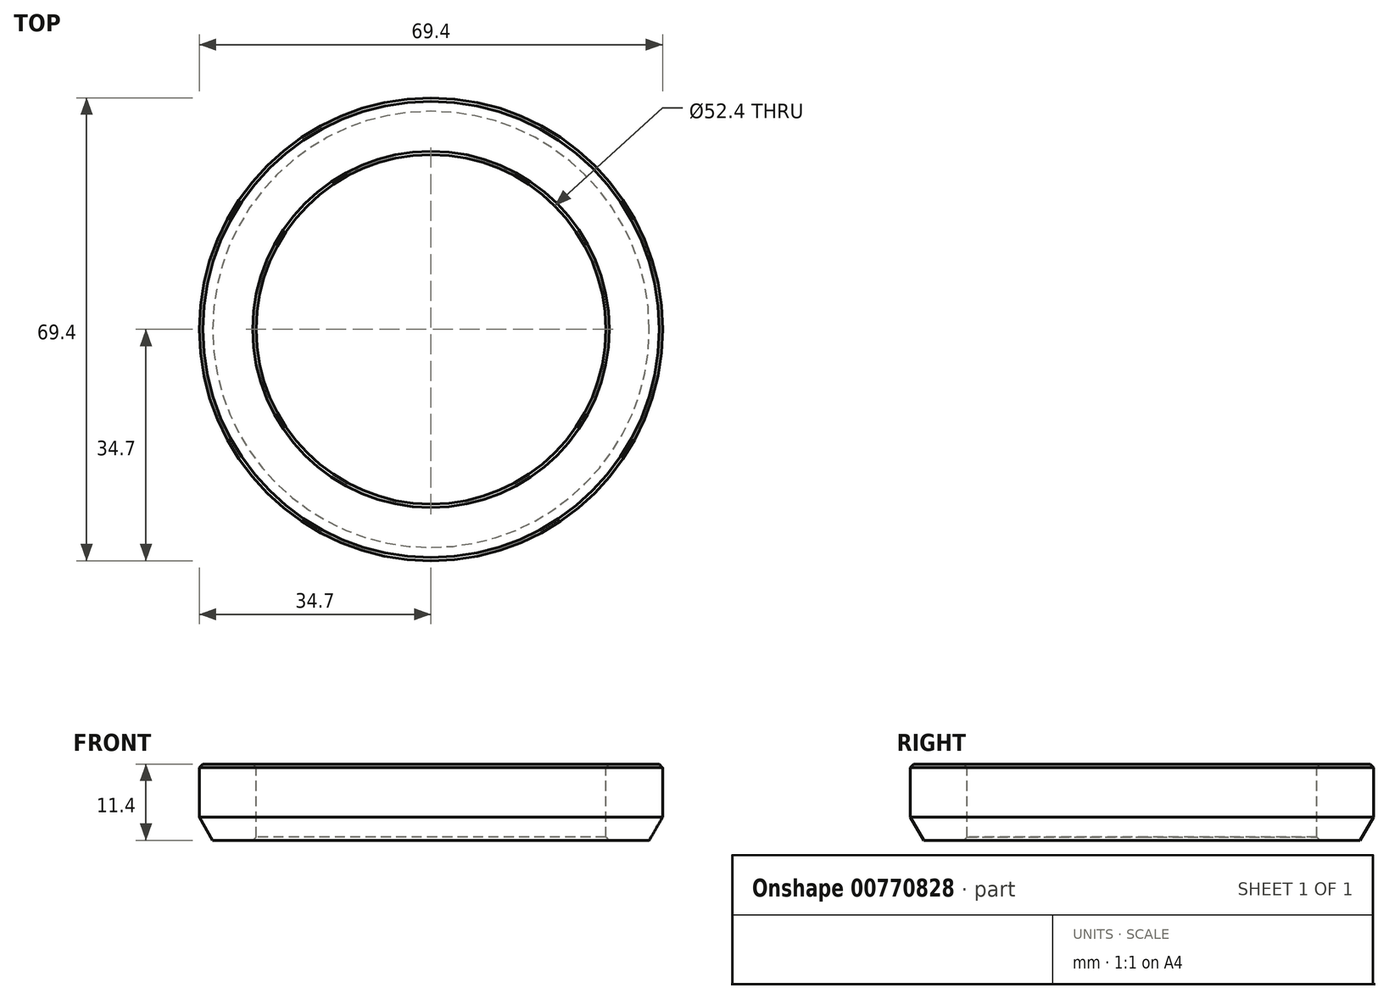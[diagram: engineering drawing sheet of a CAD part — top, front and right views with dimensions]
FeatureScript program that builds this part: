
annotation { "Feature Type Name" : "Feature", "Feature Type Description" : "" }
export const myFeature = defineFeature(function(context is Context, id is Id, definition is map)
    precondition{}
    {
        {
            var Q0;
            Q0=qCreatedBy(makeId("Front.planeOp"),FACE);
            var sketch = newSketch(context, id + "F0", { "sketchPlane" : qUnion([Q0])});
            skLineSegment(sketch, "E0", {"start": v(0, 172.54) * mm, "end": v(0, 0) * mm, "construction": true});
            skLineSegment(sketch, "E1", {"start": v(0, 0) * mm, "end": v(168.47, 0) * mm, "construction": true});
            skLineSegment(sketch, "E2.bottom", {"start": v(-26.2, 0) * mm, "end": v(-32.7, 0) * mm});
            skLineSegment(sketch, "E2.top", {"start": v(-26.2, 11.4) * mm, "end": v(-34.7, 11.4) * mm});
            skLineSegment(sketch, "E2.left", {"start": v(-26.2, 0) * mm, "end": v(-26.2, 11.4) * mm});
            skLineSegment(sketch, "E2.right", {"start": v(-34.7, 3.46) * mm, "end": v(-34.7, 11.4) * mm});
            skLineSegment(sketch, "E3", {"start": v(-34.7, 3.46) * mm, "end": v(-32.7, 0) * mm});
            skPoint(sketch, "E4.orphan", {"position": v(-34.7, 0) * mm});
            skSolve(sketch);
        }
        {
            var Q0;
            Q0=makeQuery(id+"F0.imprint","IMPRINT",FACE,{"disambiguationData":[TD([[makeQuery(id+"F0.imprint","IMPRINT",EDGE,{"derivedFrom":sQuery(id+"F0.wireOp",EDGE,"E2.bottom")}),-1.0]])]});
            var Q1;
            Q1=sQuery(id+"F0.wireOp",EDGE,"E0");
            revolve(context, id + "F1", {"surfaceOperationType" : NewSurfaceOperationType.NEW, "entities" : qUnion([Q0]), "axis" : qUnion([Q1]), "revolveType" : RevolveType.FULL});
        }
        {
            var Q0;
            Q0=makeQuery(id+"F1.opRevolve","SWEPT_EDGE",EDGE,{"disambiguationData":[OSD([sQuery(id+"F0.wireOp",EDGE,"E2.top"),sQuery(id+"F0.wireOp",EDGE,"E2.left")])]});
            var Q1;
            Q1=makeQuery(id+"F1.opRevolve","SWEPT_EDGE",EDGE,{"disambiguationData":[OSD([sQuery(id+"F0.wireOp",EDGE,"E2.top"),sQuery(id+"F0.wireOp",EDGE,"E2.right")])]});
            var Q2;
            Q2=makeQuery(id+"F1.opRevolve","SWEPT_EDGE",EDGE,{"disambiguationData":[OSD([sQuery(id+"F0.wireOp",EDGE,"E2.bottom"),sQuery(id+"F0.wireOp",EDGE,"E2.left")])]});
            chamfer(context, id + "F2", {"entities" : qUnion([Q0, Q1, Q2]), "width" : .5 * mm, "tangentPropagation" : true});
        }
    });
